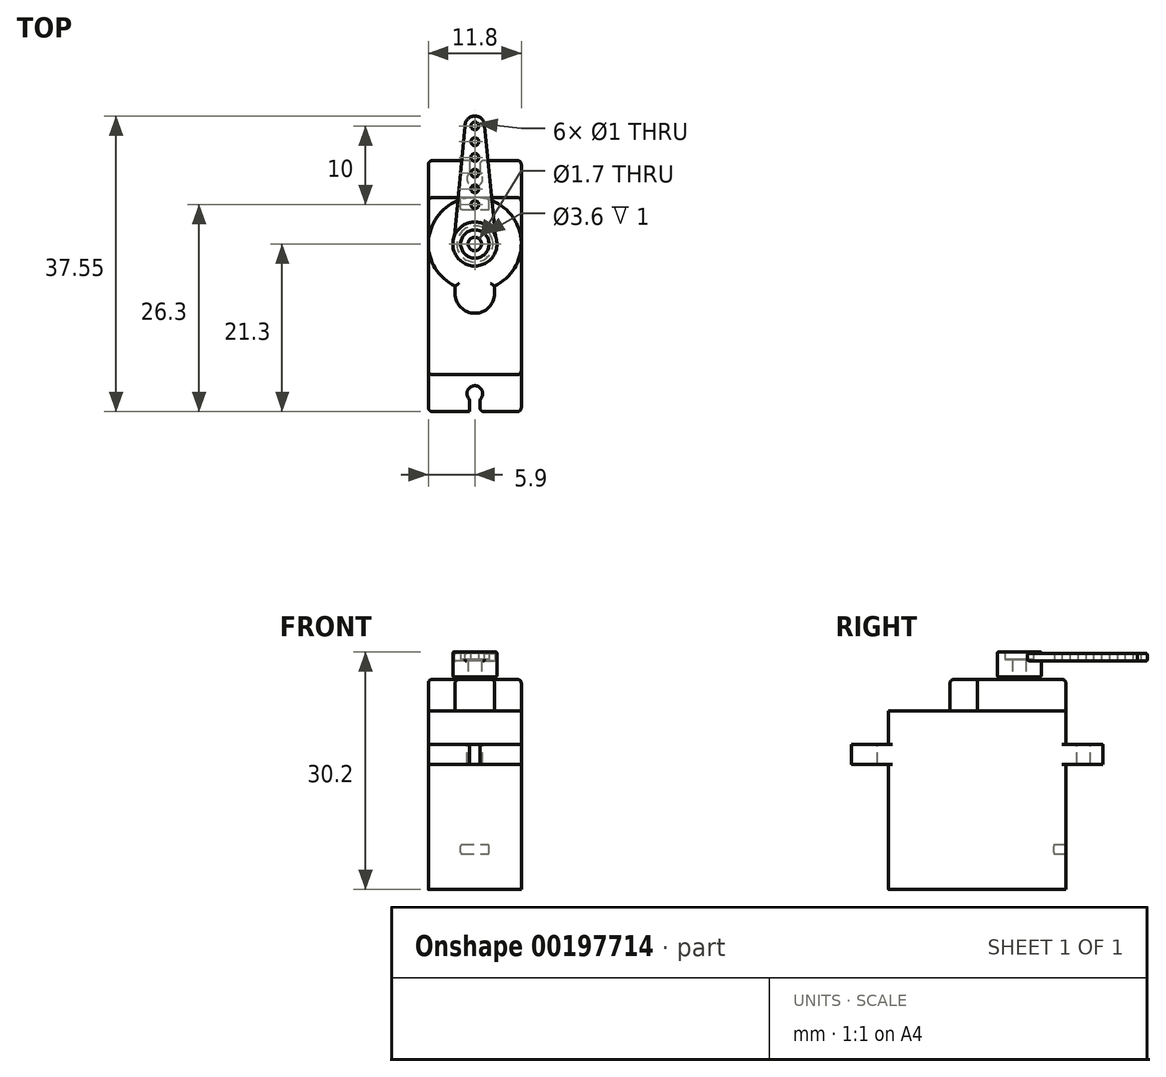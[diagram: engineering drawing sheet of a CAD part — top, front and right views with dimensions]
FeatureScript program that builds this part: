
annotation { "Feature Type Name" : "Feature", "Feature Type Description" : "" }
export const myFeature = defineFeature(function(context is Context, id is Id, definition is map)
    precondition{}
    {
        {
            var Q0;
            Q0=qCreatedBy(makeId("Right.planeOp"),FACE);
            var sketch = newSketch(context, id + "F0", { "sketchPlane" : qUnion([Q0])});
            skLineSegment(sketch, "E0.bottom", {"start": v(11.25, -11.35) * mm, "end": v(-11.25, -11.35) * mm});
            skLineSegment(sketch, "E0.top", {"start": v(11.25, 11.35) * mm, "end": v(-11.25, 11.35) * mm});
            skLineSegment(sketch, "E0.left", {"start": v(11.25, -11.35) * mm, "end": v(11.25, 11.35) * mm});
            skLineSegment(sketch, "E0.right", {"start": v(-11.25, -11.35) * mm, "end": v(-11.25, 11.35) * mm});
            skPoint(sketch, "E0.middle", {"position": v(0, 0) * mm});
            skLineSegment(sketch, "E1.bottom", {"start": v(15.95, 7.05) * mm, "end": v(-15.95, 7.05) * mm});
            skLineSegment(sketch, "E1.top", {"start": v(15.95, 4.55) * mm, "end": v(-15.95, 4.55) * mm});
            skLineSegment(sketch, "E1.left", {"start": v(15.95, 7.05) * mm, "end": v(15.95, 4.55) * mm});
            skLineSegment(sketch, "E1.right", {"start": v(-15.95, 7.05) * mm, "end": v(-15.95, 4.55) * mm});
            skPoint(sketch, "E1.middle", {"position": v(0, 5.8) * mm});
            skSolve(sketch);
        }
        {
            var Q0;
            Q0 = qSketchRegion(id + "F0", true);
            extrude(context, id + "F1", {"entities" : qUnion([Q0]), "endBound" : BoundingType.SYMMETRIC, "depth" : 11.8 * mm});
        }
        {
            var Q0;
            {var subQ0=sQuery(id+"F0.wireOp",EDGE,"E1.bottom");Q0=makeQuery(id+"F1.opExtrude","SWEPT_FACE",FACE,{"disambiguationData":[OSD([subQ0]),TDD([makeQuery(id+"F0.imprint","IMPRINT",EDGE,{"disambiguationData":[TD([[makeQuery(id+"F0.imprint","INTERSECT",VERTEX,{"derivedFrom":[subQ0,sQuery(id+"F0.wireOp",EDGE,"E1.left")]}),-1.0]])],"derivedFrom":subQ0})])]});}
            var sketch = newSketch(context, id + "F2", { "sketchPlane" : qUnion([Q0])});
            skLineSegment(sketch, "E2", {"start": v(0, 15.95) * mm, "end": v(0, -15.95) * mm, "construction": true});
            skLineSegment(sketch, "E3", {"start": v(7.37, 0) * mm, "end": v(-7.6, 0) * mm, "construction": true});
            skLineSegment(sketch, "E4.0", {"start": v(5.9, -15.95) * mm, "end": v(-5.9, -15.95) * mm});
            skCircle(sketch, "E5", {"center": v(0, 13.65) * mm, "radius": 1 * mm});
            skCircle(sketch, "E6.MirrorC", {"center": v(0, -13.65) * mm, "radius": 1 * mm});
            skLineSegment(sketch, "E7.bottom", {"start": v(-0.65, 15.95) * mm, "end": v(0.65, 15.95) * mm});
            skLineSegment(sketch, "E7.top", {"start": v(-0.65, 13.35) * mm, "end": v(0.65, 13.35) * mm});
            skLineSegment(sketch, "E7.left", {"start": v(-0.65, 15.95) * mm, "end": v(-0.65, 13.35) * mm});
            skLineSegment(sketch, "E7.right", {"start": v(0.65, 15.95) * mm, "end": v(0.65, 13.35) * mm});
            skPoint(sketch, "E7.middle", {"position": v(0, 14.65) * mm});
            skLineSegment(sketch, "E8.MirrorCS", {"start": v(0.65, -15.95) * mm, "end": v(0.65, -13.35) * mm});
            skLineSegment(sketch, "E9.MirrorCS", {"start": v(-0.65, -15.95) * mm, "end": v(-0.65, -13.35) * mm});
            skLineSegment(sketch, "E10.MirrorCS", {"start": v(-0.65, -15.95) * mm, "end": v(0.65, -15.95) * mm});
            skLineSegment(sketch, "E11.MirrorCS", {"start": v(-0.65, -13.35) * mm, "end": v(0.65, -13.35) * mm});
            skSolve(sketch);
        }
        {
            var Q0;
            Q0 = qSketchRegion(id + "F2", true);
            extrude(context, id + "F3", {"entities" : qUnion([Q0]), "operationType" : NewBodyOperationType.REMOVE, "endBound" : BoundingType.UP_TO_NEXT, "oppositeDirection" : true, "depth" : 25 * mm});
        }
        {
            var Q0;
            Q0=makeQuery(id+"F1.opExtrude","SWEPT_FACE",FACE,{"disambiguationData":[OSD([sQuery(id+"F0.wireOp",EDGE,"E0.top")])]});
            var sketch = newSketch(context, id + "F4", { "sketchPlane" : qUnion([Q0])});
            skCircle(sketch, "E12", {"center": v(0, 5.35) * mm, "radius": 5.9 * mm});
            skPoint(sketch, "E13", {"position": v(0, 11.25) * mm});
            skArc(sketch, "E14", {"start": v(-2.5, -0.95) * mm, "mid": v(0, -3.45) * mm, "end": v(2.5, -0.95) * mm});
            skPoint(sketch, "E15", {"position": v(0, -3.45) * mm});
            skLineSegment(sketch, "E16", {"start": v(2.5, -0.95) * mm, "end": v(-2.5, -0.95) * mm, "construction": true});
            skLineSegment(sketch, "E17", {"start": v(-2.5, -0.95) * mm, "end": v(-2.5, 0) * mm});
            skLineSegment(sketch, "E18", {"start": v(2.5, -0.95) * mm, "end": v(2.5, 0) * mm});
            skSolve(sketch);
        }
        {
            var Q0;
            {var subQ0=sQuery(id+"F4.wireOp",EDGE,"E12");var subQ1=makeQuery(id+"F4.imprint","INTERSECT",VERTEX,{"derivedFrom":[subQ0,sQuery(id+"F4.wireOp",EDGE,"E17")]});Q0=makeQuery(id+"F4.imprint","IMPRINT",FACE,{"disambiguationData":[TD([[makeQuery(id+"F4.imprint","IMPRINT",EDGE,{"disambiguationData":[TD([[subQ1,1.0]])],"derivedFrom":subQ0}),1.0]])]});}
            var Q1;
            Q1=makeQuery(id+"F4.imprint","IMPRINT",FACE,{"disambiguationData":[TD([[makeQuery(id+"F4.imprint","IMPRINT",EDGE,{"derivedFrom":sQuery(id+"F4.wireOp",EDGE,"E14")}),1.0]])]});
            extrude(context, id + "F5", {"entities" : qUnion([Q0, Q1]), "operationType" : NewBodyOperationType.ADD, "depth" : 4 * mm});
        }
        {
            var Q0;
            {var subQ0=sQuery(id+"F0.wireOp",EDGE,"E0.left");Q0=makeQuery(id+"F1.opExtrude","CAP_EDGE",EDGE,{"disambiguationData":[OSD([subQ0]),TDD([makeQuery(id+"F0.imprint","IMPRINT",EDGE,{"disambiguationData":[TD([[makeQuery(id+"F0.imprint","INTERSECT",VERTEX,{"derivedFrom":[sQuery(id+"F0.wireOp",EDGE,"E0.bottom"),subQ0]}),-1.0]])],"derivedFrom":subQ0})])],"isStart":true});}
            var Q1;
            {var subQ0=sQuery(id+"F0.wireOp",EDGE,"E0.left");Q1=makeQuery(id+"F1.opExtrude","CAP_EDGE",EDGE,{"disambiguationData":[OSD([subQ0]),TDD([makeQuery(id+"F0.imprint","IMPRINT",EDGE,{"disambiguationData":[TD([[makeQuery(id+"F0.imprint","INTERSECT",VERTEX,{"derivedFrom":[sQuery(id+"F0.wireOp",EDGE,"E0.top"),subQ0]}),1.0]])],"derivedFrom":subQ0})])],"isStart":true});}
            var Q2;
            {var subQ0=sQuery(id+"F0.wireOp",EDGE,"E0.left");Q2=makeQuery(id+"F1.opExtrude","CAP_EDGE",EDGE,{"disambiguationData":[OSD([subQ0]),TDD([makeQuery(id+"F0.imprint","IMPRINT",EDGE,{"disambiguationData":[TD([[makeQuery(id+"F0.imprint","INTERSECT",VERTEX,{"derivedFrom":[sQuery(id+"F0.wireOp",EDGE,"E0.bottom"),subQ0]}),-1.0]])],"derivedFrom":subQ0})])],"isStart":false});}
            var Q3;
            {var subQ0=sQuery(id+"F0.wireOp",EDGE,"E0.left");Q3=makeQuery(id+"F1.opExtrude","CAP_EDGE",EDGE,{"disambiguationData":[OSD([subQ0]),TDD([makeQuery(id+"F0.imprint","IMPRINT",EDGE,{"disambiguationData":[TD([[makeQuery(id+"F0.imprint","INTERSECT",VERTEX,{"derivedFrom":[sQuery(id+"F0.wireOp",EDGE,"E0.top"),subQ0]}),1.0]])],"derivedFrom":subQ0})])],"isStart":false});}
            var Q4;
            {var subQ0=sQuery(id+"F0.wireOp",EDGE,"E0.right");Q4=makeQuery(id+"F1.opExtrude","CAP_EDGE",EDGE,{"disambiguationData":[OSD([subQ0]),TDD([makeQuery(id+"F0.imprint","IMPRINT",EDGE,{"disambiguationData":[TD([[makeQuery(id+"F0.imprint","INTERSECT",VERTEX,{"derivedFrom":[sQuery(id+"F0.wireOp",EDGE,"E0.bottom"),subQ0]}),-1.0]])],"derivedFrom":subQ0})])],"isStart":true});}
            var Q5;
            {var subQ0=sQuery(id+"F0.wireOp",EDGE,"E0.right");Q5=makeQuery(id+"F1.opExtrude","CAP_EDGE",EDGE,{"disambiguationData":[OSD([subQ0]),TDD([makeQuery(id+"F0.imprint","IMPRINT",EDGE,{"disambiguationData":[TD([[makeQuery(id+"F0.imprint","INTERSECT",VERTEX,{"derivedFrom":[sQuery(id+"F0.wireOp",EDGE,"E0.top"),subQ0]}),1.0]])],"derivedFrom":subQ0})])],"isStart":true});}
            var Q6;
            {var subQ0=sQuery(id+"F0.wireOp",EDGE,"E0.right");Q6=makeQuery(id+"F1.opExtrude","CAP_EDGE",EDGE,{"disambiguationData":[OSD([subQ0]),TDD([makeQuery(id+"F0.imprint","IMPRINT",EDGE,{"disambiguationData":[TD([[makeQuery(id+"F0.imprint","INTERSECT",VERTEX,{"derivedFrom":[sQuery(id+"F0.wireOp",EDGE,"E0.top"),subQ0]}),1.0]])],"derivedFrom":subQ0})])],"isStart":false});}
            var Q7;
            {var subQ0=sQuery(id+"F0.wireOp",EDGE,"E0.right");Q7=makeQuery(id+"F1.opExtrude","CAP_EDGE",EDGE,{"disambiguationData":[OSD([subQ0]),TDD([makeQuery(id+"F0.imprint","IMPRINT",EDGE,{"disambiguationData":[TD([[makeQuery(id+"F0.imprint","INTERSECT",VERTEX,{"derivedFrom":[sQuery(id+"F0.wireOp",EDGE,"E0.bottom"),subQ0]}),-1.0]])],"derivedFrom":subQ0})])],"isStart":false});}
            fillet(context, id + "F6", {"entities" : qUnion([Q0, Q1, Q2, Q3, Q4, Q5, Q6, Q7]), "radius" : 0.5 * mm, "tangentPropagation" : true, "allowEdgeOverflow" : false});
        }
        {
            var Q0;
            Q0=makeQuery(id+"F1.opExtrude","CAP_EDGE",EDGE,{"disambiguationData":[OSD([sQuery(id+"F0.wireOp",EDGE,"E1.right")])],"isStart":true});
            var Q1;
            Q1=makeQuery(id+"F1.opExtrude","CAP_EDGE",EDGE,{"disambiguationData":[OSD([sQuery(id+"F0.wireOp",EDGE,"E1.right")])],"isStart":false});
            var Q2;
            Q2=makeQuery(id+"F1.opExtrude","CAP_EDGE",EDGE,{"disambiguationData":[OSD([sQuery(id+"F0.wireOp",EDGE,"E1.left")])],"isStart":true});
            var Q3;
            Q3=makeQuery(id+"F1.opExtrude","CAP_EDGE",EDGE,{"disambiguationData":[OSD([sQuery(id+"F0.wireOp",EDGE,"E1.left")])],"isStart":false});
            var Q4;
            Q4=makeQuery(id+"F3.boolean.opBoolean","COPY",EDGE,{"derivedFrom":makeQuery(id+"F3.opExtrude","SWEPT_EDGE",EDGE,{"disambiguationData":[OSD([sQuery(id+"F0.wireOp",EDGE,"E1.bottom"),sQuery(id+"F0.wireOp",EDGE,"E1.left"),sQuery(id+"F2.wireOp",EDGE,"E7.bottom"),sQuery(id+"F2.wireOp",EDGE,"E7.left")])]})});
            var Q5;
            Q5=makeQuery(id+"F3.boolean.opBoolean","COPY",EDGE,{"derivedFrom":makeQuery(id+"F3.opExtrude","SWEPT_EDGE",EDGE,{"disambiguationData":[OSD([sQuery(id+"F0.wireOp",EDGE,"E1.bottom"),sQuery(id+"F0.wireOp",EDGE,"E1.left"),sQuery(id+"F2.wireOp",EDGE,"E7.bottom"),sQuery(id+"F2.wireOp",EDGE,"E7.right")])]})});
            var Q6;
            Q6=makeQuery(id+"F3.boolean.opBoolean","COPY",EDGE,{"derivedFrom":makeQuery(id+"F3.opExtrude","SWEPT_EDGE",EDGE,{"disambiguationData":[OSD([sQuery(id+"F2.wireOp",EDGE,"E9.MirrorCS"),sQuery(id+"F2.wireOp",EDGE,"E10.MirrorCS")])]})});
            var Q7;
            Q7=makeQuery(id+"F3.boolean.opBoolean","COPY",EDGE,{"derivedFrom":makeQuery(id+"F3.opExtrude","SWEPT_EDGE",EDGE,{"disambiguationData":[OSD([sQuery(id+"F2.wireOp",EDGE,"E8.MirrorCS"),sQuery(id+"F2.wireOp",EDGE,"E10.MirrorCS")])]})});
            fillet(context, id + "F7", {"entities" : qUnion([Q0, Q1, Q2, Q3, Q4, Q5, Q6, Q7]), "radius" : 0.5 * mm, "tangentPropagation" : true, "allowEdgeOverflow" : false});
        }
        {
            var Q0;
            Q0=makeQuery(id+"F5.opExtrude","CAP_EDGE",EDGE,{"disambiguationData":[OSD([sQuery(id+"F4.wireOp",EDGE,"E12")])],"isStart":false});
            var Q1;
            Q1=makeQuery(id+"F5.opExtrude","CAP_EDGE",EDGE,{"disambiguationData":[OSD([sQuery(id+"F4.wireOp",EDGE,"E17")])],"isStart":false});
            fillet(context, id + "F8", {"entities" : qUnion([Q0, Q1]), "radius" : 0.5 * mm, "tangentPropagation" : true, "allowEdgeOverflow" : false});
        }
        {
            var Q0;
            Q0=makeQuery(id+"F5.opExtrude","CAP_FACE",FACE,{"disambiguationData":[OSD([sQuery(id+"F4.wireOp",EDGE,"E12")])],"isStart":false});
            var sketch = newSketch(context, id + "F9", { "sketchPlane" : qUnion([Q0])});
            skCircle(sketch, "E19", {"center": v(0, 5.35) * mm, "radius": 2.3 * mm});
            skCircle(sketch, "E20", {"center": v(0, 5.35) * mm, "radius": 0.85 * mm});
            skSolve(sketch);
        }
        {
            var Q0;
            Q0 = qSketchRegion(id + "F9", true);
            extrude(context, id + "F10", {"entities" : qUnion([Q0]), "depth" : 2.5 * mm});
        }
        {
            var Q0;
            Q0=makeQuery(id+"F10.opExtrude","CAP_FACE",FACE,{"disambiguationData":[OSD([sQuery(id+"F9.wireOp",EDGE,"E19")])],"isStart":false});
            var sketch = newSketch(context, id + "F11", { "sketchPlane" : qUnion([Q0])});
            skCircle(sketch, "E21", {"center": v(0, 5.35) * mm, "radius": 2.8 * mm});
            skCircle(sketch, "E22.0", {"center": v(0, 5.35) * mm, "radius": 2.3 * mm});
            skCircle(sketch, "E23", {"center": v(0, 5.35) * mm, "radius": 1.8 * mm});
            skSolve(sketch);
        }
        {
            var Q0;
            {var subQ0=sQuery(id+"F0.wireOp",EDGE,"E0.left");Q0=makeQuery(id+"F1.opExtrude","SWEPT_FACE",FACE,{"disambiguationData":[OSD([subQ0]),TDD([makeQuery(id+"F0.imprint","IMPRINT",EDGE,{"disambiguationData":[TD([[makeQuery(id+"F0.imprint","INTERSECT",VERTEX,{"derivedFrom":[sQuery(id+"F0.wireOp",EDGE,"E0.bottom"),subQ0]}),-1.0]])],"derivedFrom":subQ0})])]});}
            var sketch = newSketch(context, id + "F12", { "sketchPlane" : qUnion([Q0])});
            skLineSegment(sketch, "E24.0", {"start": v(5.9, 4.55) * mm, "end": v(5.9, -11.35) * mm});
            skLineSegment(sketch, "E25.0", {"start": v(-5.9, -11.35) * mm, "end": v(-5.9, 4.55) * mm});
            skLineSegment(sketch, "E26.bottom", {"start": v(1.8, -6.85) * mm, "end": v(-1.8, -6.85) * mm});
            skLineSegment(sketch, "E26.top", {"start": v(1.8, -5.65) * mm, "end": v(-1.8, -5.65) * mm});
            skLineSegment(sketch, "E26.left", {"start": v(1.8, -6.85) * mm, "end": v(1.8, -5.65) * mm});
            skLineSegment(sketch, "E26.right", {"start": v(-1.8, -6.85) * mm, "end": v(-1.8, -5.65) * mm});
            skPoint(sketch, "E26.middle", {"position": v(0, -6.25) * mm});
            skPoint(sketch, "E26.middle.positionSnap0", {"position": v(0, -11.35) * mm});
            skPoint(sketch, "E26.centerSnap0", {"position": v(0, -11.35) * mm});
            skSolve(sketch);
        }
        {
            var Q0;
            Q0 = qSketchRegion(id + "F12", true);
            extrude(context, id + "F13", {"entities" : qUnion([Q0]), "operationType" : NewBodyOperationType.REMOVE, "oppositeDirection" : true, "depth" : 1.5 * mm});
        }
        {
            var Q0;
            Q0=makeQuery(id+"F13.boolean.opBoolean","COPY",EDGE,{"derivedFrom":makeQuery(id+"F13.opExtrude","SWEPT_EDGE",EDGE,{"disambiguationData":[OSD([sQuery(id+"F12.wireOp",EDGE,"E26.bottom"),sQuery(id+"F12.wireOp",EDGE,"E26.right")])]})});
            var Q1;
            Q1=makeQuery(id+"F13.boolean.opBoolean","COPY",EDGE,{"derivedFrom":makeQuery(id+"F13.opExtrude","SWEPT_EDGE",EDGE,{"disambiguationData":[OSD([sQuery(id+"F12.wireOp",EDGE,"E26.bottom"),sQuery(id+"F12.wireOp",EDGE,"E26.left")])]})});
            var Q2;
            Q2=makeQuery(id+"F13.boolean.opBoolean","COPY",EDGE,{"derivedFrom":makeQuery(id+"F13.opExtrude","SWEPT_EDGE",EDGE,{"disambiguationData":[OSD([sQuery(id+"F12.wireOp",EDGE,"E26.top"),sQuery(id+"F12.wireOp",EDGE,"E26.left")])]})});
            var Q3;
            Q3=makeQuery(id+"F13.boolean.opBoolean","COPY",EDGE,{"derivedFrom":makeQuery(id+"F13.opExtrude","SWEPT_EDGE",EDGE,{"disambiguationData":[OSD([sQuery(id+"F12.wireOp",EDGE,"E26.top"),sQuery(id+"F12.wireOp",EDGE,"E26.right")])]})});
            fillet(context, id + "F14", {"entities" : qUnion([Q0, Q1, Q2, Q3]), "radius" : 0.2 * mm, "tangentPropagation" : true, "allowEdgeOverflow" : false});
        }
        {
            var Q0;
            Q0=makeQuery(id+"F11.imprint","IMPRINT",FACE,{"disambiguationData":[TD([[makeQuery(id+"F11.imprint","IMPRINT",EDGE,{"derivedFrom":sQuery(id+"F11.wireOp",EDGE,"E21")}),1.0]])]});
            extrude(context, id + "F15", {"entities" : qUnion([Q0]), "oppositeDirection" : true, "depth" : 2.2 * mm, "hasSecondDirection" : true, "secondDirectionOppositeDirection" : false, "secondDirectionDepth" : 1 * mm});
        }
        {
            var Q0;
            Q0=makeQuery(id+"F11.imprint","IMPRINT",FACE,{"disambiguationData":[TD([[makeQuery(id+"F11.imprint","IMPRINT",EDGE,{"derivedFrom":sQuery(id+"F11.wireOp",EDGE,"E22.0")}),1.0]])]});
            extrude(context, id + "F16", {"entities" : qUnion([Q0]), "operationType" : NewBodyOperationType.ADD, "depth" : 1 * mm});
        }
        {
            var Q0;
            {var subQ0=sQuery(id+"F11.wireOp",EDGE,"E22.0");Q0=makeQuery(id+"F16.boolean.opBoolean","MERGE",FACE,{"derivedFrom":[makeQuery(id+"F15.opExtrude","CAP_FACE",FACE,{"disambiguationData":[OSD([sQuery(id+"F11.wireOp",EDGE,"E21"),subQ0])],"isStart":true}),makeQuery(id+"F16.opExtrude","CAP_FACE",FACE,{"disambiguationData":[OSD([subQ0,sQuery(id+"F11.wireOp",EDGE,"E23")])],"isStart":false})]});}
            var sketch = newSketch(context, id + "F17", { "sketchPlane" : qUnion([Q0])});
            skLineSegment(sketch, "E27", {"start": v(0, 5.35) * mm, "end": v(0, 20.35) * mm, "construction": true});
            skCircle(sketch, "E28", {"center": v(0, 20.35) * mm, "radius": 1.25 * mm});
            skCircle(sketch, "E29.0", {"center": v(0, 5.35) * mm, "radius": 2.8 * mm});
            skCircle(sketch, "E30", {"center": v(0, 10.35) * mm, "radius": 0.5 * mm});
            skLineSegment(sketch, "E31", {"start": v(-1.25, 20.35) * mm, "end": v(-2.61, 6.36) * mm});
            skLineSegment(sketch, "E32.MirrorCS", {"start": v(1.25, 20.35) * mm, "end": v(2.61, 6.36) * mm});
            skCircle(sketch, "E33", {"center": v(0, 12.35) * mm, "radius": 0.5 * mm});
            skCircle(sketch, "E34", {"center": v(0, 14.35) * mm, "radius": 0.5 * mm});
            skCircle(sketch, "E35", {"center": v(0, 16.35) * mm, "radius": 0.5 * mm});
            skCircle(sketch, "E36", {"center": v(0, 18.35) * mm, "radius": 0.5 * mm});
            skCircle(sketch, "E37", {"center": v(0, 20.35) * mm, "radius": 0.5 * mm});
            skSolve(sketch);
        }
        {
            var Q0;
            Q0=makeQuery(id+"F17.imprint","IMPRINT",FACE,{"disambiguationData":[TD([[makeQuery(id+"F17.imprint","IMPRINT",EDGE,{"derivedFrom":sQuery(id+"F17.wireOp",EDGE,"E30")}),-1.0]])]});
            var Q1;
            {var subQ0=sQuery(id+"F17.wireOp",EDGE,"E28");var subQ1=makeQuery(id+"F17.imprint","INTERSECT",VERTEX,{"derivedFrom":[subQ0,sQuery(id+"F17.wireOp",EDGE,"E31")]});Q1=makeQuery(id+"F17.imprint","IMPRINT",FACE,{"disambiguationData":[TD([[makeQuery(id+"F17.imprint","IMPRINT",EDGE,{"disambiguationData":[TD([[subQ1,1.0]])],"derivedFrom":subQ0}),1.0]])]});}
            extrude(context, id + "F18", {"entities" : qUnion([Q0, Q1]), "operationType" : NewBodyOperationType.ADD, "oppositeDirection" : true, "depth" : 1.2 * mm, "hasSecondDirection" : true, "secondDirectionOppositeDirection" : true, "secondDirectionDepth" : 0.2 * mm});
        }
        {
            var Q0;
            Q0=makeQuery(id+"F15.opExtrude","CAP_EDGE",EDGE,{"disambiguationData":[OSD([sQuery(id+"F11.wireOp",EDGE,"E21")])],"isStart":true});
            fillet(context, id + "F19", {"entities" : qUnion([Q0]), "radius" : 0.2 * mm, "tangentPropagation" : true, "allowEdgeOverflow" : false});
        }
        {
            var Q0;
            Q0=makeQuery(id+"F18.opExtrude","CAP_EDGE",EDGE,{"disambiguationData":[OSD([sQuery(id+"F17.wireOp",EDGE,"E31")])],"isStart":true});
            var Q1;
            Q1=makeQuery(id+"F18.opExtrude","CAP_EDGE",EDGE,{"disambiguationData":[OSD([sQuery(id+"F17.wireOp",EDGE,"E32.MirrorCS")])],"isStart":true});
            var Q2;
            Q2=makeQuery(id+"F18.opExtrude","CAP_EDGE",EDGE,{"disambiguationData":[OSD([sQuery(id+"F17.wireOp",EDGE,"E31")])],"isStart":false});
            var Q3;
            Q3=makeQuery(id+"F18.opExtrude","CAP_EDGE",EDGE,{"disambiguationData":[OSD([sQuery(id+"F17.wireOp",EDGE,"E32.MirrorCS")])],"isStart":false});
            var Q4;
            Q4=makeQuery(id+"F18.opExtrude","CAP_EDGE",EDGE,{"disambiguationData":[OSD([sQuery(id+"F17.wireOp",EDGE,"E28")])],"isStart":true});
            var Q5;
            Q5=makeQuery(id+"F18.opExtrude","CAP_EDGE",EDGE,{"disambiguationData":[OSD([sQuery(id+"F17.wireOp",EDGE,"E28")])],"isStart":false});
            fillet(context, id + "F20", {"entities" : qUnion([Q0, Q1, Q2, Q3, Q4, Q5]), "radius" : 0.2 * mm, "tangentPropagation" : true, "allowEdgeOverflow" : false});
        }
        {
            var Q0;
            Q0=makeQuery(id+"F15.opExtrude","CAP_EDGE",EDGE,{"disambiguationData":[OSD([sQuery(id+"F11.wireOp",EDGE,"E21")])],"isStart":false});
            fillet(context, id + "F21", {"entities" : qUnion([Q0]), "radius" : 0.2 * mm, "tangentPropagation" : true, "allowEdgeOverflow" : false});
        }
    });
